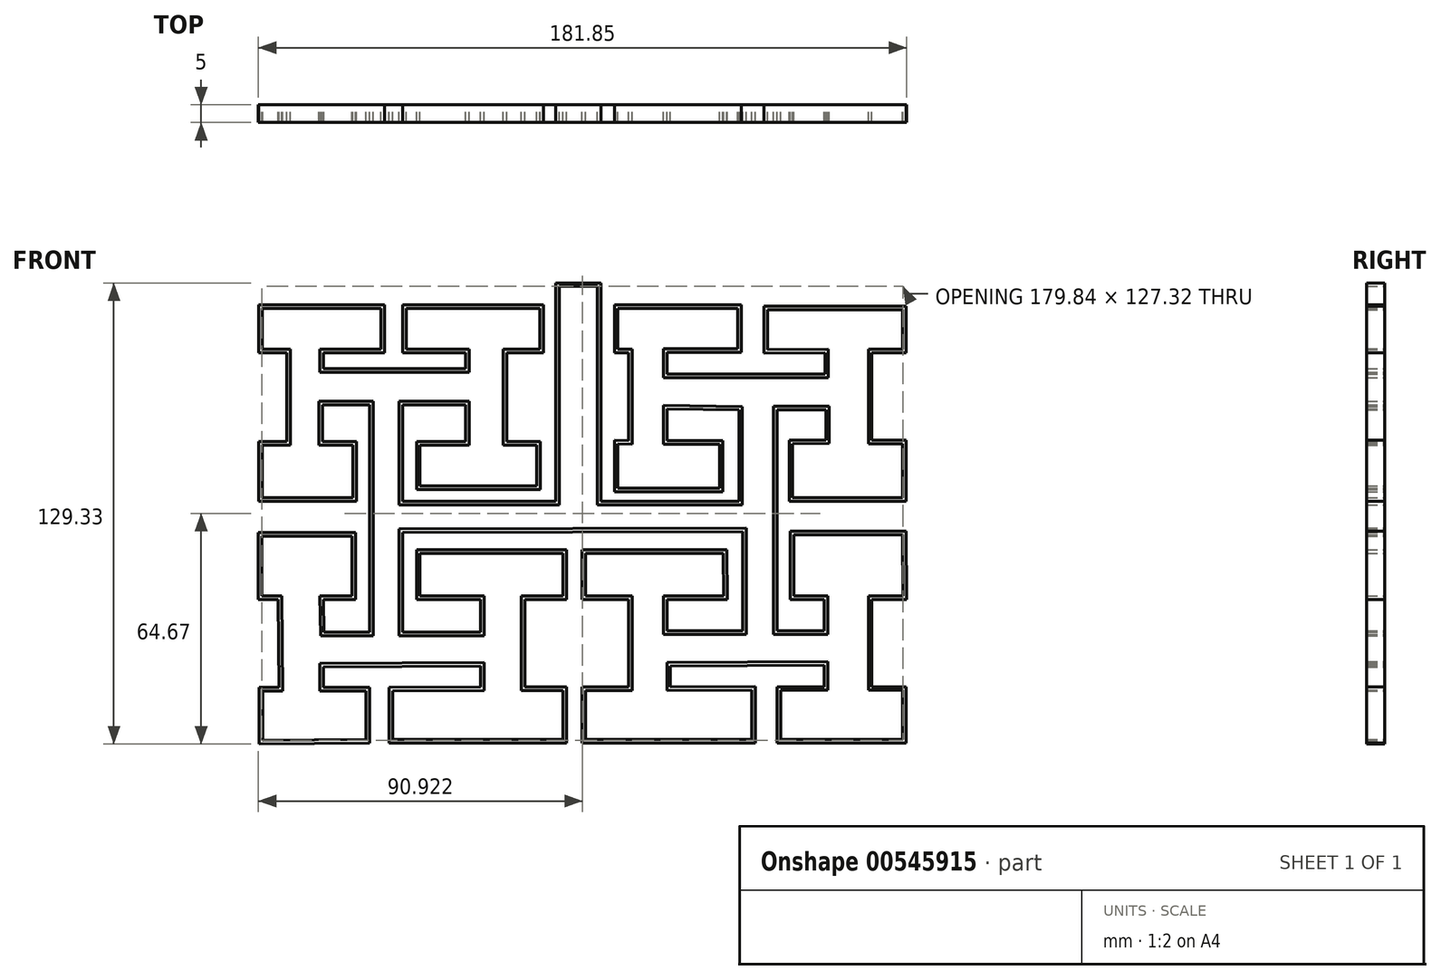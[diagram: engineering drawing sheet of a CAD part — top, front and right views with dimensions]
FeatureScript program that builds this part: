
annotation { "Feature Type Name" : "Feature", "Feature Type Description" : "" }
export const myFeature = defineFeature(function(context is Context, id is Id, definition is map)
    precondition{}
    {
        {
            var Q0;
            Q0=qCreatedBy(makeId("Front.planeOp"),FACE);
            var sketch = newSketch(context, id + "F0", { "sketchPlane" : qUnion([Q0])});
            skLineSegment(sketch, "E0", {"start": v(-2.88, 52.14) * mm, "end": v(-2.88, -9.1) * mm});
            skLineSegment(sketch, "E1", {"start": v(-2.88, -9.1) * mm, "end": v(-45.82, -9.1) * mm});
            skLineSegment(sketch, "E2", {"start": v(-45.82, -9.1) * mm, "end": v(-45.82, 17.9) * mm});
            skLineSegment(sketch, "E3", {"start": v(-45.82, 17.9) * mm, "end": v(-28.12, 17.9) * mm});
            skLineSegment(sketch, "E4", {"start": v(-28.12, 32.48) * mm, "end": v(-28.12, 28.07) * mm});
            skLineSegment(sketch, "E5", {"start": v(-55.12, 17.9) * mm, "end": v(-55.12, -45.88) * mm});
            skLineSegment(sketch, "E6", {"start": v(49.52, -17.67) * mm, "end": v(49.52, -45.43) * mm});
            skLineSegment(sketch, "E7", {"start": v(59.23, -45.43) * mm, "end": v(59.23, 16.49) * mm});
            skLineSegment(sketch, "E8", {"start": v(59.23, 16.49) * mm, "end": v(72.86, 16.49) * mm});
            skLineSegment(sketch, "E9", {"start": v(72.6, 26.6) * mm, "end": v(28.32, 26.6) * mm});
            skLineSegment(sketch, "E10", {"start": v(28.32, 7.9) * mm, "end": v(28.32, 16.77) * mm});
            skLineSegment(sketch, "E11", {"start": v(28.32, 16.77) * mm, "end": v(48.48, 16.49) * mm});
            skLineSegment(sketch, "E12", {"start": v(48.48, 16.49) * mm, "end": v(48.48, -9.1) * mm});
            skLineSegment(sketch, "E13", {"start": v(48.48, -9.1) * mm, "end": v(9.83, -9.1) * mm});
            skLineSegment(sketch, "E14", {"start": v(9.83, -9.1) * mm, "end": v(9.83, 52.14) * mm});
            skLineSegment(sketch, "E15", {"start": v(9.83, 52.14) * mm, "end": v(-2.88, 52.14) * mm});
            skLineSegment(sketch, "E16", {"start": v(59.23, -45.43) * mm, "end": v(59.23, -45.43) * mm});
            skLineSegment(sketch, "E17", {"start": v(49.52, -45.43) * mm, "end": v(28.32, -45.43) * mm});
            skLineSegment(sketch, "E18", {"start": v(28.32, -45.43) * mm, "end": v(28.32, -36.72) * mm});
            skLineSegment(sketch, "E19", {"start": v(59.23, -45.43) * mm, "end": v(72.44, -45.43) * mm});
            skLineSegment(sketch, "E20", {"start": v(72.44, -45.43) * mm, "end": v(72.44, -36.72) * mm});
            skLineSegment(sketch, "E21", {"start": v(72.44, -55.06) * mm, "end": v(29.28, -55.39) * mm});
            skLineSegment(sketch, "E22", {"start": v(29.28, -55.39) * mm, "end": v(29.28, -61.15) * mm});
            skLineSegment(sketch, "E23", {"start": v(17.57, -61.2) * mm, "end": v(17.57, -36.72) * mm});
            skLineSegment(sketch, "E24", {"start": v(-23.97, -45.88) * mm, "end": v(-23.97, -36.72) * mm});
            skLineSegment(sketch, "E25", {"start": v(-23.97, -61.2) * mm, "end": v(-23.97, -55.39) * mm});
            skLineSegment(sketch, "E26", {"start": v(-23.97, -55.39) * mm, "end": v(-68.04, -55.55) * mm});
            skLineSegment(sketch, "E27", {"start": v(-80.55, -61.28) * mm, "end": v(-80.74, -36.72) * mm});
            skLineSegment(sketch, "E28", {"start": v(-68.04, -36.72) * mm, "end": v(-67.87, -45.88) * mm});
            skLineSegment(sketch, "E29", {"start": v(-67.87, -45.88) * mm, "end": v(-55.12, -45.88) * mm});
            skLineSegment(sketch, "E30", {"start": v(-28.12, 28.07) * mm, "end": v(-68.04, 28.07) * mm});
            skLineSegment(sketch, "E31", {"start": v(-68.04, 28.07) * mm, "end": v(-68.04, 32.48) * mm});
            skLineSegment(sketch, "E32", {"start": v(-68.32, 17.9) * mm, "end": v(-55.12, 17.9) * mm});
            skLineSegment(sketch, "E33", {"start": v(-68.32, 17.9) * mm, "end": v(-68.32, 7.64) * mm});
            skLineSegment(sketch, "E34", {"start": v(-68.32, 7.64) * mm, "end": v(-58.8, 7.64) * mm});
            skLineSegment(sketch, "E35", {"start": v(-86.2, 7.64) * mm, "end": v(-78.35, 7.64) * mm});
            skLineSegment(sketch, "E36", {"start": v(-78.35, 32.48) * mm, "end": v(-78.35, 7.64) * mm});
            skLineSegment(sketch, "E37", {"start": v(-59.05, -36.72) * mm, "end": v(-68.04, -36.72) * mm});
            skLineSegment(sketch, "E38", {"start": v(-23.97, -36.72) * mm, "end": v(-41.95, -36.72) * mm});
            skLineSegment(sketch, "E39", {"start": v(-41.95, -36.72) * mm, "end": v(-41.95, -22.68) * mm});
            skLineSegment(sketch, "E40", {"start": v(4.5, -22.67) * mm, "end": v(45.11, -22.67) * mm});
            skLineSegment(sketch, "E41", {"start": v(45.11, -22.67) * mm, "end": v(45.22, -36.72) * mm});
            skLineSegment(sketch, "E42", {"start": v(45.22, -36.72) * mm, "end": v(28.32, -36.72) * mm});
            skLineSegment(sketch, "E43", {"start": v(17.57, 7.93) * mm, "end": v(13.55, 7.97) * mm});
            skPoint(sketch, "E44.endSnap0", {"position": v(38.4, 16.63) * mm});
            skLineSegment(sketch, "E45", {"start": v(13.55, 7.97) * mm, "end": v(13.55, -6.43) * mm});
            skLineSegment(sketch, "E46", {"start": v(-41.95, -22.68) * mm, "end": v(0.1, -22.68) * mm});
            skLineSegment(sketch, "E47", {"start": v(-11.54, -61.2) * mm, "end": v(0.1, -61.2) * mm});
            skLineSegment(sketch, "E48", {"start": v(95.4, -61.15) * mm, "end": v(85.8, -61.15) * mm});
            skLineSegment(sketch, "E49", {"start": v(-45.87, -17.84) * mm, "end": v(49.52, -17.67) * mm});
            skLineSegment(sketch, "E50", {"start": v(62.9, -17.52) * mm, "end": v(62.9, -36.72) * mm});
            skLineSegment(sketch, "E51", {"start": v(62.9, -36.72) * mm, "end": v(72.44, -36.72) * mm});
            skLineSegment(sketch, "E52", {"start": v(95.53, -36.72) * mm, "end": v(85.8, -36.71) * mm});
            skLineSegment(sketch, "E53", {"start": v(85.8, -36.71) * mm, "end": v(85.8, -61.15) * mm});
            skLineSegment(sketch, "E54", {"start": v(4.5, -22.67) * mm, "end": v(4.5, -36.72) * mm});
            skLineSegment(sketch, "E55", {"start": v(4.5, -36.72) * mm, "end": v(17.57, -36.72) * mm});
            skLineSegment(sketch, "E56", {"start": v(-11.54, -61.2) * mm, "end": v(-11.54, -36.72) * mm});
            skLineSegment(sketch, "E57", {"start": v(-11.54, -36.72) * mm, "end": v(0.1, -36.72) * mm});
            skLineSegment(sketch, "E58", {"start": v(0.1, -36.72) * mm, "end": v(0.1, -22.68) * mm});
            skLineSegment(sketch, "E59", {"start": v(-86.32, -36.72) * mm, "end": v(-80.74, -36.72) * mm});
            skLineSegment(sketch, "E60", {"start": v(-6.36, 45.95) * mm, "end": v(-6.36, 32.48) * mm});
            skLineSegment(sketch, "E61", {"start": v(-16.63, 7.64) * mm, "end": v(-7.2, 7.64) * mm});
            skLineSegment(sketch, "E62", {"start": v(-7.2, 7.64) * mm, "end": v(-7.2, -5.76) * mm});
            skLineSegment(sketch, "E63", {"start": v(-28.12, 17.9) * mm, "end": v(-28.12, 7.64) * mm});
            skLineSegment(sketch, "E64", {"start": v(-41.95, 7.64) * mm, "end": v(-28.12, 7.64) * mm});
            skLineSegment(sketch, "E65", {"start": v(-41.95, 7.64) * mm, "end": v(-41.95, -5.76) * mm});
            skLineSegment(sketch, "E66", {"start": v(-41.95, -5.76) * mm, "end": v(-7.2, -5.76) * mm});
            skLineSegment(sketch, "E67", {"start": v(85.8, 8.06) * mm, "end": v(95.36, 8.06) * mm});
            skLineSegment(sketch, "E68", {"start": v(17.57, 7.93) * mm, "end": v(17.57, 32.48) * mm});
            skLineSegment(sketch, "E69", {"start": v(72.6, 32.48) * mm, "end": v(72.6, 26.6) * mm});
            skLineSegment(sketch, "E70", {"start": v(28.32, 32.64) * mm, "end": v(28.32, 26.6) * mm});
            skLineSegment(sketch, "E71", {"start": v(95.36, 45.6) * mm, "end": v(95.36, 32.48) * mm});
            skLineSegment(sketch, "E72", {"start": v(95.36, 32.48) * mm, "end": v(85.8, 32.48) * mm});
            skLineSegment(sketch, "E73", {"start": v(85.8, 32.48) * mm, "end": v(85.8, 8.06) * mm});
            skLineSegment(sketch, "E74", {"start": v(28.32, 7.9) * mm, "end": v(44, 7.9) * mm});
            skLineSegment(sketch, "E75", {"start": v(44, 7.9) * mm, "end": v(44, -6.43) * mm});
            skLineSegment(sketch, "E76", {"start": v(44, -6.43) * mm, "end": v(13.55, -6.43) * mm});
            skLineSegment(sketch, "E77", {"start": v(62.9, -17.52) * mm, "end": v(95.36, -17.52) * mm});
            skLineSegment(sketch, "E78", {"start": v(95.36, -17.52) * mm, "end": v(95.53, -36.72) * mm});
            skLineSegment(sketch, "E79", {"start": v(62.58, 7.97) * mm, "end": v(62.58, -9.1) * mm});
            skLineSegment(sketch, "E80", {"start": v(95.36, -9.1) * mm, "end": v(95.36, 8.06) * mm});
            skLineSegment(sketch, "E81", {"start": v(95.36, -9.1) * mm, "end": v(62.58, -9.1) * mm});
            skLineSegment(sketch, "E82", {"start": v(-86.2, 7.64) * mm, "end": v(-86.2, -9.1) * mm});
            skPoint(sketch, "E82.endSnap0", {"position": v(29.15, -9.1) * mm});
            skLineSegment(sketch, "E83", {"start": v(-86.2, -9.1) * mm, "end": v(-58.8, -9.1) * mm});
            skLineSegment(sketch, "E84", {"start": v(-58.8, -9.1) * mm, "end": v(-58.8, 7.64) * mm});
            skLineSegment(sketch, "E85", {"start": v(-59.05, -36.72) * mm, "end": v(-59.05, -17.84) * mm});
            skLineSegment(sketch, "E86", {"start": v(-59.05, -17.84) * mm, "end": v(-86.32, -17.84) * mm});
            skLineSegment(sketch, "E87", {"start": v(-86.32, -17.84) * mm, "end": v(-86.32, -36.72) * mm});
            skLineSegment(sketch, "E88", {"start": v(-23.97, -61.2) * mm, "end": v(-49.66, -61.28) * mm});
            skLineSegment(sketch, "E89", {"start": v(-86.09, -77.2) * mm, "end": v(-55.16, -76.88) * mm});
            skLineSegment(sketch, "E90", {"start": v(-55.12, -61.28) * mm, "end": v(-55.16, -76.88) * mm});
            skLineSegment(sketch, "E91", {"start": v(-49.66, -61.28) * mm, "end": v(-49.66, -76.88) * mm});
            skLineSegment(sketch, "E92", {"start": v(-49.66, -76.88) * mm, "end": v(0.1, -76.88) * mm});
            skLineSegment(sketch, "E93", {"start": v(0.1, -61.2) * mm, "end": v(0.1, -76.88) * mm});
            skLineSegment(sketch, "E94", {"start": v(17.57, -61.2) * mm, "end": v(4.5, -61.2) * mm});
            skLineSegment(sketch, "E95", {"start": v(4.5, -61.2) * mm, "end": v(4.5, -76.88) * mm});
            skLineSegment(sketch, "E96", {"start": v(95.4, -61.15) * mm, "end": v(95.4, -76.88) * mm});
            skLineSegment(sketch, "E97", {"start": v(59.23, -61.15) * mm, "end": v(59.23, -76.88) * mm});
            skLineSegment(sketch, "E98", {"start": v(59.23, -76.88) * mm, "end": v(95.4, -76.88) * mm});
            skLineSegment(sketch, "E99", {"start": v(59.23, -61.15) * mm, "end": v(72.44, -61.15) * mm});
            skLineSegment(sketch, "E100", {"start": v(72.44, -61.15) * mm, "end": v(72.44, -55.06) * mm});
            skLineSegment(sketch, "E101", {"start": v(-86.2, 45.95) * mm, "end": v(-86.2, 32.48) * mm});
            skLineSegment(sketch, "E102", {"start": v(-86.2, 32.48) * mm, "end": v(-78.35, 32.48) * mm});
            skLineSegment(sketch, "E103", {"start": v(-6.36, 32.48) * mm, "end": v(-16.63, 32.48) * mm});
            skLineSegment(sketch, "E104", {"start": v(-16.63, 32.48) * mm, "end": v(-16.63, 7.64) * mm});
            skLineSegment(sketch, "E105", {"start": v(13.55, 45.95) * mm, "end": v(13.55, 32.48) * mm});
            skLineSegment(sketch, "E106", {"start": v(13.55, 32.48) * mm, "end": v(17.57, 32.48) * mm});
            skLineSegment(sketch, "E107", {"start": v(-68.04, -55.55) * mm, "end": v(-68.04, -61.28) * mm});
            skLineSegment(sketch, "E108", {"start": v(-68.04, -61.28) * mm, "end": v(-55.12, -61.28) * mm});
            skLineSegment(sketch, "E109", {"start": v(-80.55, -61.28) * mm, "end": v(-86.09, -61.33) * mm});
            skLineSegment(sketch, "E110", {"start": v(-86.09, -61.33) * mm, "end": v(-86.09, -77.2) * mm});
            skLineSegment(sketch, "E111", {"start": v(72.86, 16.49) * mm, "end": v(72.86, 8.06) * mm});
            skLineSegment(sketch, "E112", {"start": v(72.86, 8.06) * mm, "end": v(62.58, 7.97) * mm});
            skLineSegment(sketch, "E113", {"start": v(29.28, -61.15) * mm, "end": v(53.04, -61.1) * mm});
            skLineSegment(sketch, "E114", {"start": v(53.04, -61.1) * mm, "end": v(53.04, -76.88) * mm});
            skLineSegment(sketch, "E115", {"start": v(53.04, -76.88) * mm, "end": v(4.5, -76.88) * mm});
            skLineSegment(sketch, "E116", {"start": v(-23.97, -45.88) * mm, "end": v(-45.82, -45.88) * mm});
            skLineSegment(sketch, "E117", {"start": v(-45.82, -45.88) * mm, "end": v(-45.87, -17.84) * mm});
            skLineSegment(sketch, "E118", {"start": v(72.6, 32.48) * mm, "end": v(55.5, 32.39) * mm});
            skLineSegment(sketch, "E119", {"start": v(55.5, 32.39) * mm, "end": v(55.5, 45.6) * mm});
            skLineSegment(sketch, "E120", {"start": v(55.5, 45.6) * mm, "end": v(95.36, 45.6) * mm});
            skLineSegment(sketch, "E121", {"start": v(28.32, 32.64) * mm, "end": v(49.15, 32.64) * mm});
            skLineSegment(sketch, "E122", {"start": v(49.15, 32.64) * mm, "end": v(49.15, 45.95) * mm});
            skLineSegment(sketch, "E123", {"start": v(13.55, 45.95) * mm, "end": v(49.15, 45.95) * mm});
            skLineSegment(sketch, "E124", {"start": v(-68.04, 32.48) * mm, "end": v(-50.93, 32.48) * mm});
            skLineSegment(sketch, "E125", {"start": v(-50.93, 32.48) * mm, "end": v(-50.93, 45.95) * mm});
            skLineSegment(sketch, "E126", {"start": v(-86.2, 45.95) * mm, "end": v(-50.93, 45.95) * mm});
            skLineSegment(sketch, "E127", {"start": v(-28.12, 32.48) * mm, "end": v(-45.78, 32.48) * mm});
            skLineSegment(sketch, "E128", {"start": v(-45.78, 32.48) * mm, "end": v(-45.78, 45.95) * mm});
            skLineSegment(sketch, "E129", {"start": v(-6.36, 45.95) * mm, "end": v(-45.78, 45.95) * mm});
            skSolve(sketch);
        }
        {
            var Q0;
            Q0=qSketchRegion(id+"F0",true);
            extrude(context, id + "F1", {"entities" : qUnion([Q0]), "depth" : 5 * mm, "offsetDistance" : 25 * mm});
        }
        {
            var Q0;
            Q0=makeQuery(id+"F1.opExtrude","CAP_FACE",FACE,{"disambiguationData":[OSD([sQuery(id+"F0.wireOp",EDGE,"E0"),sQuery(id+"F0.wireOp",EDGE,"E1"),sQuery(id+"F0.wireOp",EDGE,"E2"),sQuery(id+"F0.wireOp",EDGE,"E3"),sQuery(id+"F0.wireOp",EDGE,"0rGJifHI-jr66-wbDg-rM8z-Gyrml041EVCU"),sQuery(id+"F0.wireOp",EDGE,"O5gZCwZo-5vPl-gXqo-gQuE-8HRGq8jhTCgY"),sQuery(id+"F0.wireOp",EDGE,"hElFucvx-IacZ-mgPS-t7yp-cj8InfuzOnlj"),sQuery(id+"F0.wireOp",EDGE,"Uhj9fsSP-xh4G-2w61-e7PG-lvGmQOlik4t5"),sQuery(id+"F0.wireOp",EDGE,"sH9atn1R-PntD-0juO-QIdX-bAtbbOQWvYwp"),sQuery(id+"F0.wireOp",EDGE,"oQomcRs6-VDuB-sYYi-fSPW-H2Tfd0qEHbaM"),sQuery(id+"F0.wireOp",EDGE,"UnowPzTY-xZr5-7Aet-b9ej-U1rt1Gu2egCq"),sQuery(id+"F0.wireOp",EDGE,"yyQZgFFz-2k0r-PoZb-v5ri-RnsavJP0LVhZ"),sQuery(id+"F0.wireOp",EDGE,"YYlCSO5O-rywH-7tDy-2e1c-VmEedtuGnNeI"),sQuery(id+"F0.wireOp",EDGE,"o7U1QUH9-Bizy-FnEP-bnXV-sUYex51NHFII"),sQuery(id+"F0.wireOp",EDGE,"3DAbgUuS-fvVc-geps-bFK8-xOxQtyu7GzQa"),sQuery(id+"F0.wireOp",EDGE,"E4"),sQuery(id+"F0.wireOp",EDGE,"IEaiaTz4-dMwO-VgY0-wrVl-V68zQjIATh8B"),sQuery(id+"F0.wireOp",EDGE,"E5"),sQuery(id+"F0.wireOp",EDGE,"pfqTZ073-mhvP-Qkyh-MUPj-TS27THIkMp0C"),sQuery(id+"F0.wireOp",EDGE,"E6"),sQuery(id+"F0.wireOp",EDGE,"4seGXC9S-5lUI-0MFB-faRe-gNnUsWFBkGLq"),sQuery(id+"F0.wireOp",EDGE,"E7"),sQuery(id+"F0.wireOp",EDGE,"E8"),sQuery(id+"F0.wireOp",EDGE,"ZPlPz8ge-dgCm-qWKU-5tTG-DJQ7y9RT0O0H"),sQuery(id+"F0.wireOp",EDGE,"E9"),sQuery(id+"F0.wireOp",EDGE,"gbrKAfxO-92AK-XEcJ-9OpR-hcoryFF79E04"),sQuery(id+"F0.wireOp",EDGE,"3vezzqAC-wAgj-fnDP-g2lt-PDv5F4YDJ1Mo"),sQuery(id+"F0.wireOp",EDGE,"qiSCz8MD-0VgE-bjD9-nINq-wrJv7cMU0vCl"),sQuery(id+"F0.wireOp",EDGE,"E10"),sQuery(id+"F0.wireOp",EDGE,"E11"),sQuery(id+"F0.wireOp",EDGE,"E12"),sQuery(id+"F0.wireOp",EDGE,"E13"),sQuery(id+"F0.wireOp",EDGE,"E14"),sQuery(id+"F0.wireOp",EDGE,"E15"),sQuery(id+"F0.wireOp",EDGE,"xayQcVOS-liC2-hxBQ-rZ0L-SZ5zFzAhj4Ic"),sQuery(id+"F0.wireOp",EDGE,"zNBuiZSY-Xxu7-aESX-C3IH-8pzw2wy47kDA"),sQuery(id+"F0.wireOp",EDGE,"ETQssxLX-QlN4-Bsqe-sDEl-vYBZZVPnwrvs"),sQuery(id+"F0.wireOp",EDGE,"HPTRIoQK-h0lG-Q6Bk-wStF-GJtdEg2o0b1i"),sQuery(id+"F0.wireOp",EDGE,"fwiKdGGd-y9Ga-leHZ-tmYf-mcaM3Z835Oif"),sQuery(id+"F0.wireOp",EDGE,"8nCNafXq-HolM-m2JL-76AW-AiOXpf6xnWZI"),sQuery(id+"F0.wireOp",EDGE,"e8pZc5By-Qqm5-OqoQ-K9ER-PWDTnBCWdlPG")])],"isStart":false});
            shell(context, id + "F2", {"entities" : qUnion([Q0]), "thickness" : 1 * mm});
        }
        {
            var Q0;
            Q0=makeQuery(id+"F2.opShell","OFFSET_FACE",FACE,{"disambiguationData":[OSD([sQuery(id+"F0.wireOp",EDGE,"E0"),sQuery(id+"F0.wireOp",EDGE,"E1"),sQuery(id+"F0.wireOp",EDGE,"E2"),sQuery(id+"F0.wireOp",EDGE,"E3"),sQuery(id+"F0.wireOp",EDGE,"0rGJifHI-jr66-wbDg-rM8z-Gyrml041EVCU"),sQuery(id+"F0.wireOp",EDGE,"O5gZCwZo-5vPl-gXqo-gQuE-8HRGq8jhTCgY"),sQuery(id+"F0.wireOp",EDGE,"hElFucvx-IacZ-mgPS-t7yp-cj8InfuzOnlj"),sQuery(id+"F0.wireOp",EDGE,"sH9atn1R-PntD-0juO-QIdX-bAtbbOQWvYwp"),sQuery(id+"F0.wireOp",EDGE,"E4"),sQuery(id+"F0.wireOp",EDGE,"E5"),sQuery(id+"F0.wireOp",EDGE,"pfqTZ073-mhvP-Qkyh-MUPj-TS27THIkMp0C"),sQuery(id+"F0.wireOp",EDGE,"E6"),sQuery(id+"F0.wireOp",EDGE,"E7"),sQuery(id+"F0.wireOp",EDGE,"E8"),sQuery(id+"F0.wireOp",EDGE,"E9"),sQuery(id+"F0.wireOp",EDGE,"gbrKAfxO-92AK-XEcJ-9OpR-hcoryFF79E04"),sQuery(id+"F0.wireOp",EDGE,"qiSCz8MD-0VgE-bjD9-nINq-wrJv7cMU0vCl"),sQuery(id+"F0.wireOp",EDGE,"E10"),sQuery(id+"F0.wireOp",EDGE,"E11"),sQuery(id+"F0.wireOp",EDGE,"E12"),sQuery(id+"F0.wireOp",EDGE,"E13"),sQuery(id+"F0.wireOp",EDGE,"E14"),sQuery(id+"F0.wireOp",EDGE,"E15"),sQuery(id+"F0.wireOp",EDGE,"xayQcVOS-liC2-hxBQ-rZ0L-SZ5zFzAhj4Ic"),sQuery(id+"F0.wireOp",EDGE,"zNBuiZSY-Xxu7-aESX-C3IH-8pzw2wy47kDA"),sQuery(id+"F0.wireOp",EDGE,"HPTRIoQK-h0lG-Q6Bk-wStF-GJtdEg2o0b1i"),sQuery(id+"F0.wireOp",EDGE,"fwiKdGGd-y9Ga-leHZ-tmYf-mcaM3Z835Oif"),sQuery(id+"F0.wireOp",EDGE,"E17"),sQuery(id+"F0.wireOp",EDGE,"E18"),sQuery(id+"F0.wireOp",EDGE,"E19"),sQuery(id+"F0.wireOp",EDGE,"E20"),sQuery(id+"F0.wireOp",EDGE,"DF9jEozI-RnD6-uLl7-ty4W-egYaCa1YIfHE"),sQuery(id+"F0.wireOp",EDGE,"syxlt2ZS-eiO0-j3PC-kv6v-Wq7q7PEPjB7C"),sQuery(id+"F0.wireOp",EDGE,"E21"),sQuery(id+"F0.wireOp",EDGE,"E22"),sQuery(id+"F0.wireOp",EDGE,"E23"),sQuery(id+"F0.wireOp",EDGE,"4oQNBMxG-D50x-KGPy-tYlA-XOJBMoQNdo1O"),sQuery(id+"F0.wireOp",EDGE,"8NzacRhR-l8cC-oEHb-p8Dw-z8LEPdpKCXz0"),sQuery(id+"F0.wireOp",EDGE,"7pZx8a3p-xA9n-ltwE-bDZt-Vi2PgclJtaYc"),sQuery(id+"F0.wireOp",EDGE,"A5FxOgFy-1bDJ-lc5R-EMpP-DYOvTxJ1UNuw"),sQuery(id+"F0.wireOp",EDGE,"E24"),sQuery(id+"F0.wireOp",EDGE,"UCzrKhTp-UBAk-lfpO-2ii1-m7XGNqAXi1tG"),sQuery(id+"F0.wireOp",EDGE,"E25"),sQuery(id+"F0.wireOp",EDGE,"E26"),sQuery(id+"F0.wireOp",EDGE,"JSiu3OMq-eDuJ-OMIg-w7vb-mMdvukqkO2BE"),sQuery(id+"F0.wireOp",EDGE,"E27"),sQuery(id+"F0.wireOp",EDGE,"E28"),sQuery(id+"F0.wireOp",EDGE,"E29"),sQuery(id+"F0.wireOp",EDGE,"E30"),sQuery(id+"F0.wireOp",EDGE,"E31"),sQuery(id+"F0.wireOp",EDGE,"E32"),sQuery(id+"F0.wireOp",EDGE,"E33"),sQuery(id+"F0.wireOp",EDGE,"E34"),sQuery(id+"F0.wireOp",EDGE,"hcV0YMCR-aJbk-3Onp-8VU4-jEnNrGrIGtMu"),sQuery(id+"F0.wireOp",EDGE,"jBHxYlAz-Qau3-cZ75-jHaJ-kV23tUoRqWzb"),sQuery(id+"F0.wireOp",EDGE,"m3VWYkpQ-xcTO-eFW3-sDwi-de49Pc0dBjZN"),sQuery(id+"F0.wireOp",EDGE,"E35"),sQuery(id+"F0.wireOp",EDGE,"774DuTWV-BWOP-H7NW-sr8P-c7WmqvUMVwQP"),sQuery(id+"F0.wireOp",EDGE,"uAuTruCM-L9Jc-6FBC-gI6Z-WalRWmT0hNun"),sQuery(id+"F0.wireOp",EDGE,"sJAetESs-pFRC-QrjC-D6SH-wypyDsYGOn8R"),sQuery(id+"F0.wireOp",EDGE,"cUinRcM6-zbdM-kdlT-mWhU-B6XQGjpti7ya"),sQuery(id+"F0.wireOp",EDGE,"E36"),sQuery(id+"F0.wireOp",EDGE,"R3euyznr-d5Yo-p4fu-IaUM-o9fcxow5uihU"),sQuery(id+"F0.wireOp",EDGE,"wIqKh9UP-KPq9-OGsH-uzNu-P7eFrv5tuLLK"),sQuery(id+"F0.wireOp",EDGE,"eFmDLmtt-lkUK-jsLd-v5uJ-iO0F9s88OsYa"),sQuery(id+"F0.wireOp",EDGE,"ZWKULN2G-xaCB-Bh4M-IIMY-HsUB07SKP57r"),sQuery(id+"F0.wireOp",EDGE,"JaTvzter-AwAS-qe9M-51Ed-PCmYqVoZIcBH"),sQuery(id+"F0.wireOp",EDGE,"OIYGgmPv-YUsU-mKkV-OpxU-vFHl2freXu8c"),sQuery(id+"F0.wireOp",EDGE,"8hZJnTky-rwVM-JpF5-ENYt-lwa983HodMwC"),sQuery(id+"F0.wireOp",EDGE,"zLccoBm8-j5GL-aYgq-3vdZ-bJDPIgiOPSD1"),sQuery(id+"F0.wireOp",EDGE,"F7FmvLcu-tRIg-7ExO-ftbH-m8K52cDSUgoQ"),sQuery(id+"F0.wireOp",EDGE,"znVrAdfO-vwHg-AvKV-D4IN-v6yyL14VDBoS"),sQuery(id+"F0.wireOp",EDGE,"d2cwnRnI-YePD-5BW5-sH8l-S7UlOrAlKExS"),sQuery(id+"F0.wireOp",EDGE,"E37"),sQuery(id+"F0.wireOp",EDGE,"qQc8es8a-WnnM-2eez-cvJz-64dTTMnp3h0E"),sQuery(id+"F0.wireOp",EDGE,"CYvTm9JV-wheU-eKbl-nGd4-oZLCpJgl9Lnv"),sQuery(id+"F0.wireOp",EDGE,"orpq5Edt-TkCt-5Ada-y68H-t5QMboWftwUa"),sQuery(id+"F0.wireOp",EDGE,"Yx1EBUI5-qq7P-tvTn-VXEd-PxBR2B1vkviD"),sQuery(id+"F0.wireOp",EDGE,"3VoRePm4-mMbP-g77q-isid-SKkAGzUf03bW"),sQuery(id+"F0.wireOp",EDGE,"E38"),sQuery(id+"F0.wireOp",EDGE,"E39"),sQuery(id+"F0.wireOp",EDGE,"6P1THJsA-qVDB-ye86-Vt15-AGH4uJXvwRuH"),sQuery(id+"F0.wireOp",EDGE,"bKuXfP9Q-WTjT-EUzr-5F7h-iWXuLqpDcppc"),sQuery(id+"F0.wireOp",EDGE,"Q5IsP4mF-8Urt-UzEo-voyt-4D9YDuESX3ml"),sQuery(id+"F0.wireOp",EDGE,"76fEtzId-QnQ1-3nDV-x5XH-c7JqhQNPQHs1"),sQuery(id+"F0.wireOp",EDGE,"t4HqxAGo-gRE7-MpOv-DBt6-Grr4RqsdMJj5"),sQuery(id+"F0.wireOp",EDGE,"YS4KKici-eiB7-2RRp-DGdw-uwympdU4VZEW"),sQuery(id+"F0.wireOp",EDGE,"IDq8N9PN-IHWp-QuWh-ODKr-WNOeygsZBEmy"),sQuery(id+"F0.wireOp",EDGE,"C9XTPWQV-A0WL-75pT-TMFi-1Bt9hg3HrfjU"),sQuery(id+"F0.wireOp",EDGE,"Dy0VSIlR-oW3U-YAIK-advW-AMVi2TKNiAzk"),sQuery(id+"F0.wireOp",EDGE,"DRF0KekJ-OWNU-Yk6J-BttZ-MMWdoUzslnDt"),sQuery(id+"F0.wireOp",EDGE,"wZXheHjd-JIxd-j251-MmBs-Z8k9jtyUu6Xu"),sQuery(id+"F0.wireOp",EDGE,"w9wDZcGd-hsvb-d42f-ZFvA-6eSia8WWJ0IU"),sQuery(id+"F0.wireOp",EDGE,"SkW96Fqa-P3c8-zqri-nkms-5BFziZ9Pq922"),sQuery(id+"F0.wireOp",EDGE,"yhJC7IVL-Yy2p-k5y6-5ctR-HX5TejYhyha9"),sQuery(id+"F0.wireOp",EDGE,"dsmTcbEM-M4vR-qdTc-cJB3-jjcql8KVUUrS"),sQuery(id+"F0.wireOp",EDGE,"PshYRCJx-tIiU-aNs2-KFfR-FHXtgqc0vlMY"),sQuery(id+"F0.wireOp",EDGE,"jeMI6aK9-tyA1-iKcn-9ZHm-aNgQk83ykcml"),sQuery(id+"F0.wireOp",EDGE,"nUCnzmbV-cHF4-42zB-huhg-LxLUjVWuwJnS"),sQuery(id+"F0.wireOp",EDGE,"LUud77Et-SqMx-9VOB-vryO-H7XdPYHYUGit"),sQuery(id+"F0.wireOp",EDGE,"qSWgSX21-7sCQ-Cba8-rIri-IkvMKF3dYcGz"),sQuery(id+"F0.wireOp",EDGE,"E40"),sQuery(id+"F0.wireOp",EDGE,"E41"),sQuery(id+"F0.wireOp",EDGE,"E42"),sQuery(id+"F0.wireOp",EDGE,"BiKmqsoV-tuqH-NPVY-MMmZ-ogy9ulocDaS8"),sQuery(id+"F0.wireOp",EDGE,"RTecAsd1-88py-Nyi9-0y6s-IqaKTPE5627f"),sQuery(id+"F0.wireOp",EDGE,"sBGqXisA-Dofv-bauZ-Kp7W-4uMBAylpxw3N"),sQuery(id+"F0.wireOp",EDGE,"bLsUgfjm-NMRb-74sC-jdhh-21U9RXb1qZFt"),sQuery(id+"F0.wireOp",EDGE,"wxeJ7uNN-oFdR-C6I0-UmzP-4JFHdthfjzXu"),sQuery(id+"F0.wireOp",EDGE,"E43"),sQuery(id+"F0.wireOp",EDGE,"n4GdYRYW-hJs7-AgS2-2ll7-ELzc6hCOWGbY"),sQuery(id+"F0.wireOp",EDGE,"fElvyGwW-AtXi-VFy8-KfPj-MhWESGdjJg5Q"),sQuery(id+"F0.wireOp",EDGE,"zOGYT4m3-9znk-CEkP-qpxb-4ospZJNDxLl0"),sQuery(id+"F0.wireOp",EDGE,"gmprAGF9-774p-PScN-JcbL-qEcXkFvj9TKc"),sQuery(id+"F0.wireOp",EDGE,"KIGxG4NU-ZxCZ-LI1f-2d7o-Jw1mlA6w8pA0"),sQuery(id+"F0.wireOp",EDGE,"NDdeXURV-dKj3-llMP-jnmO-nDX2OQ1m4AbQ"),sQuery(id+"F0.wireOp",EDGE,"jNDkS270-Sq8a-uu6r-EeGc-jfNBrli0H21a"),sQuery(id+"F0.wireOp",EDGE,"E44"),sQuery(id+"F0.wireOp",EDGE,"VQ0GzhKa-15pq-bXWe-UmfV-VvPDsQ2ieM5S"),sQuery(id+"F0.wireOp",EDGE,"hH8Tjkyq-UvSf-z5wF-dwLc-9XRYQN1hS3py"),sQuery(id+"F0.wireOp",EDGE,"jhDEfg4C-E3C5-sL8O-8b0m-iTHqJgyC6Rdg"),sQuery(id+"F0.wireOp",EDGE,"9meZ5Gaz-H4cK-kfh0-8uad-680rmWHjwBpR"),sQuery(id+"F0.wireOp",EDGE,"N9p9aLwb-WHUc-Fm4U-s8hX-YGZU7NQUwxka"),sQuery(id+"F0.wireOp",EDGE,"kvWoCIl1-kD1B-FocN-LTuq-ZgjSrFJ03SPt"),sQuery(id+"F0.wireOp",EDGE,"Y2AG044z-kK3D-qWMP-BubC-pnxChUG2ig3y"),sQuery(id+"F0.wireOp",EDGE,"8yMbZU2G-6E4k-eqFE-7LSC-do8jI8MXBdT3"),sQuery(id+"F0.wireOp",EDGE,"RnCaBnJO-p4Ie-NBj4-Qn3O-6UY94ZlSywB4"),sQuery(id+"F0.wireOp",EDGE,"WtdvYr6K-Yhmw-pE4l-JLyk-vZSJJyKmGYaV"),sQuery(id+"F0.wireOp",EDGE,"BTjadsGZ-JXWB-5zN4-AkSP-hUxFBmYrqks0"),sQuery(id+"F0.wireOp",EDGE,"IpDpNGVN-JWAh-pXiM-4xDb-O0koVmg00roA")])]});
            extrude(context, id + "F3", {"entities" : qUnion([Q0]), "operationType" : NewBodyOperationType.REMOVE, "oppositeDirection" : true, "depth" : 25 * mm, "offsetDistance" : 25 * mm});
        }
    });
